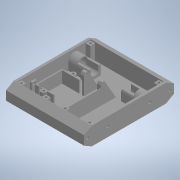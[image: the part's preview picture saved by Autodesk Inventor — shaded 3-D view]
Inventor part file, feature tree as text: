
AUTODESK INVENTOR PART (.ipt)
format: ipt  version: 2020 (Build 240168000, 168)  size: 605,184 bytes
history: native  units: in
note: dims shown in document units (in); Inventor stores cm internally (conversion verified against a paired STEP export)
features: extrude x18, sketch x17, projected_geometry x14, mirror x6, plane x1
ambient origin geometry x8: Origin, YZ Plane, XZ Plane, XY Plane, X Axis, Y Axis, Z Axis, Center Point
bodies: Solid1 (feature_tree)
feature tree (56):
  extrude  "Extrusion1"  Depth=5.9055in
  extrude  "Extrusion2"  TaperAngle=0.0deg  [1 undecoded]
  extrude  "Extrusion3"  Depth=1.063in
  extrude  "Extrusion4"  Depth=0.315in
  extrude  "Extrusion5"  TaperAngle=0.0deg  [1 undecoded]
  extrude  "Extrusion6"  Depth=0.5906in
  mirror  "Mirror1"
  extrude  "Extrusion7"  Depth=0.0787in
  mirror  "Mirror2"
  extrude  "Extrusion8"  Depth=0.6102in
  mirror  "Mirror3"
  plane  "Work Plane1"
  extrude  "Extrusion9"  Depth=0.7874in TaperAngle=0.0deg
  mirror  "Mirror4"
  extrude  "Extrusion10"  Depth=0.1654in TaperAngle=0.0deg
  extrude  "Extrusion11"  Depth=0.1575in
  extrude  "Extrusion12"  TaperAngle=0.0deg  [1 undecoded]
  extrude  "Extrusion13"  Depth=0.2756in
  extrude  "Extrusion14"  Depth=0.4331in
  extrude  "Extrusion17"  Depth=2.7559in
  extrude  "Extrusion18"  Depth=0.061in
  mirror  "Mirror6"
  extrude  "Extrusion19"  TaperAngle=0.0deg  [1 undecoded]
  mirror  "Mirror7"
  extrude  "Extrusion20"  TaperAngle=60.0deg  [1 undecoded]
  sketch  "Sketch1"  dims[d0=1.1811in d1=5.9055in]
  sketch  "Sketch2"  dims[d2=5.1181in d3=0.0in]
  projected_geometry  "Projected Loop1"
  sketch  "Sketch3"  dims[d4=0.1575in d5=1.063in]
  projected_geometry  "Projected Loop2"
  projected_geometry  "Projected Loop3"
  sketch  "Sketch4"  dims[d6=0.0in d8=0.315in]
  projected_geometry  "Projected Loop4"
  sketch  "Sketch6"  dims[d10=0.993in d11=0.0in]
  sketch  "Sketch7"  dims[d12=0.6496in d13=0.5906in]
  sketch  "Sketch9"  dims[d14=1.5748in d15=0.0787in]
  sketch  "Sketch10"  dims[d16=0.5512in d17=0.0in d18=0.6102in]
  sketch  "Sketch12"  dims[d19=0.4803in d20=0.7874in d21=0.0in]
  projected_geometry  "Projected Loop6"
  projected_geometry  "Projected Loop7"
  projected_geometry  "Projected Loop8"
  sketch  "Sketch13"  dims[d22=0.1654in d23=6.063in d24=0.0in]
  sketch  "Sketch14"  dims[d25=0.5114in d26=0.1575in]
  sketch  "Sketch15"  dims[d27=1.5748in d28=0.0in d29=0.0in]
  projected_geometry  "Projected Loop15"
  sketch  "Sketch16"  dims[d30=0.1575in d31=0.2756in]
  projected_geometry  "Projected Loop19"
  projected_geometry  "Projected Loop20"
  projected_geometry  "Projected Loop21"
  projected_geometry  "Projected Loop22"
  projected_geometry  "Projected Loop23"
  projected_geometry  "Projected Loop24"
  sketch  "Sketch20"  dims[d32=0.0in d33=0.4331in]
  sketch  "Sketch21"  dims[d34=0.122in d38=2.7559in]
  sketch  "Sketch22"  dims[d40=0.061in d41=0.0909in]
  sketch  "Sketch23"  dims[d42=0.2362in d43=0.0in d44=60.0deg d45=0.0787in d46=0.315in d48=0.993in d49=0.0in d53=0.2756in d54=0.0in d55=0.4724in d56=1.2008in d57=1.6142in d58=1.5945in d59=0.0787in d60=0.0787in d62=0.315in d63=0.7677in d64=0.0in d66=0.1476in d67=0.2756in d68=0.0in d69=0.7874in d70=0.2953in d71=0.1181in d72=0.0in d89=0.0157in d90=0.0157in d91=0.1476in d92=0.1476in d96=0.315in d97=0.1575in d98=0.1181in d99=0.0in d102=0.1772in d104=0.3346in d105=135.0deg d106=0.2362in d107=0.0in d108=0.0394in d109=0.0in d110=0.0315in d111=0.0394in d112=0.0in]
note: 5 required parameter values undecoded (feature->parameter linkage not recoverable at this tier; creation-order binding heuristic only, values carry confidence <= 0.55)
